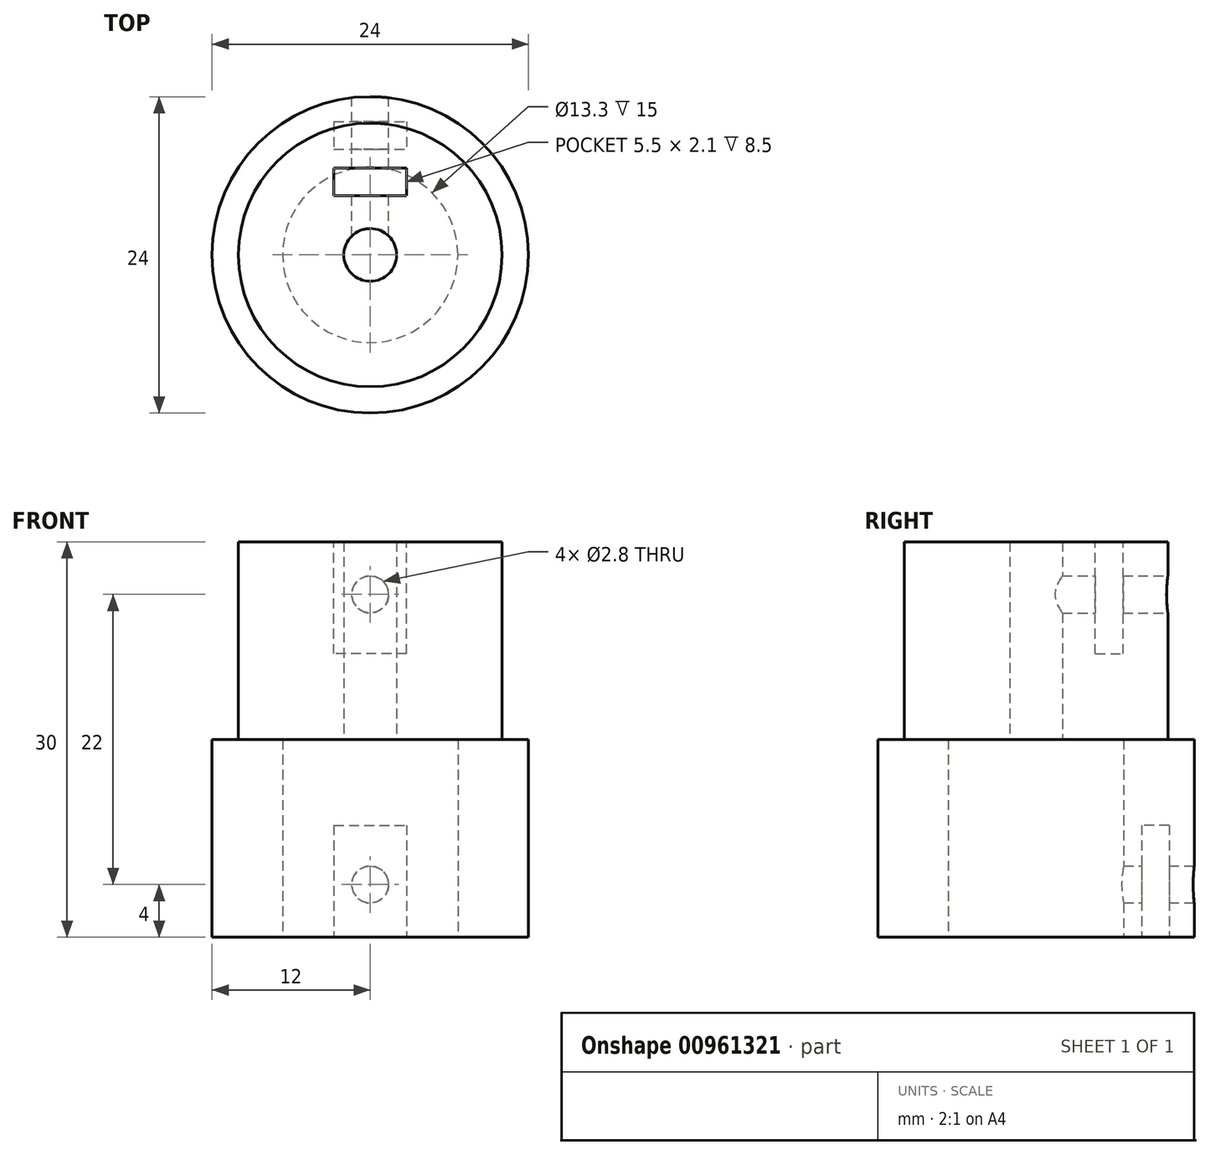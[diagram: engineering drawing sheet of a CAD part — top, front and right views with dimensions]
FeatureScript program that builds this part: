
annotation { "Feature Type Name" : "Feature", "Feature Type Description" : "" }
export const myFeature = defineFeature(function(context is Context, id is Id, definition is map)
    precondition{}
    {
        {
            var Q0;
            Q0=qCreatedBy(makeId("Top.planeOp"),FACE);
            var sketch = newSketch(context, id + "F0", { "sketchPlane" : qUnion([Q0])});
            skCircle(sketch, "E0", {"center": v(0, 0) * mm, "radius": 6.65 * mm});
            skCircle(sketch, "E1", {"center": v(0, 0) * mm, "radius": 12 * mm});
            skSolve(sketch);
        }
        {
            var Q0;
            Q0 = qSketchRegion(id + "F0", true);
            extrude(context, id + "F1", {"entities" : qUnion([Q0]), "depth" : 15 * mm, "offsetDistance" : 25 * mm});
        }
        {
            var Q0;
            Q0=qCreatedBy(makeId("Front.planeOp"),FACE);
            cPlane(context, id + "F2", {"entities" : qUnion([Q0]), "cplaneType" : CPlaneType.OFFSET, "offset" : 14 * mm, "oppositeDirection" : true, "width" : 150 * mm, "height" : 150 * mm});
        }
        {
            var Q0;
            Q0=qCreatedBy(id+"F2.planeOp",FACE);
            var sketch = newSketch(context, id + "F3", { "sketchPlane" : qUnion([Q0])});
            skCircle(sketch, "E2", {"center": v(0, 4) * mm, "radius": 1.4 * mm});
            skSolve(sketch);
        }
        {
            var Q0;
            Q0=makeQuery(id+"F3.imprint","IMPRINT",FACE,{"disambiguationData":[TD([[makeQuery(id+"F3.imprint","IMPRINT",EDGE,{"derivedFrom":sQuery(id+"F3.wireOp",EDGE,"E2")}),1.0]])]});
            var Q1;
            Q1=makeQuery(id+"F3.imprint","IMPRINT",FACE,{"disambiguationData":[TD([[makeQuery(id+"F3.imprint","IMPRINT",EDGE,{"derivedFrom":sQuery(id+"F3.wireOp",EDGE,"FONxLhb4-qUyD-SSOe-wBW2-8P9LQDapAw2D")}),1.0]])]});
            extrude(context, id + "F4", {"entities" : qUnion([Q0, Q1]), "operationType" : NewBodyOperationType.REMOVE, "depth" : 10 * mm, "offsetDistance" : 25 * mm});
        }
        {
            var Q0;
            Q0=makeQuery(id+"F1.opExtrude","CAP_FACE",FACE,{"disambiguationData":[OSD([sQuery(id+"F0.wireOp",EDGE,"E0"),sQuery(id+"F0.wireOp",EDGE,"E1")])],"isStart":false});
            var sketch = newSketch(context, id + "F5", { "sketchPlane" : qUnion([Q0])});
            skCircle(sketch, "E3", {"center": v(0, 0) * mm, "radius": 10 * mm});
            skCircle(sketch, "E4", {"center": v(0, 0) * mm, "radius": 2 * mm});
            skSolve(sketch);
        }
        {
            var Q0;
            Q0 = qSketchRegion(id + "F5", true);
            extrude(context, id + "F6", {"entities" : qUnion([Q0]), "operationType" : NewBodyOperationType.ADD, "depth" : 15 * mm, "offsetDistance" : 25 * mm});
        }
        {
            var Q0;
            Q0=qCreatedBy(makeId("Front.planeOp"),FACE);
            cPlane(context, id + "F7", {"entities" : qUnion([Q0]), "cplaneType" : CPlaneType.OFFSET, "offset" : 11.5 * mm, "oppositeDirection" : true, "width" : 150 * mm, "height" : 150 * mm});
        }
        {
            var Q0;
            Q0=qCreatedBy(id+"F7.planeOp",FACE);
            var sketch = newSketch(context, id + "F8", { "sketchPlane" : qUnion([Q0])});
            skCircle(sketch, "E5", {"center": v(0, 26) * mm, "radius": 1.4 * mm});
            skSolve(sketch);
        }
        {
            var Q0;
            Q0 = qSketchRegion(id + "F8", true);
            extrude(context, id + "F9", {"entities" : qUnion([Q0]), "operationType" : NewBodyOperationType.REMOVE, "depth" : 11 * mm, "offsetDistance" : 25 * mm});
        }
        {
            var Q0;
            Q0=makeQuery(id+"F6.opExtrude","CAP_FACE",FACE,{"disambiguationData":[OSD([sQuery(id+"F5.wireOp",EDGE,"E3"),sQuery(id+"F5.wireOp",EDGE,"E4")])],"isStart":false});
            var sketch = newSketch(context, id + "F10", { "sketchPlane" : qUnion([Q0])});
            skLineSegment(sketch, "E6.bottom", {"start": v(2.75, 4.5) * mm, "end": v(-2.75, 4.5) * mm});
            skLineSegment(sketch, "E6.top", {"start": v(2.75, 6.6) * mm, "end": v(-2.75, 6.6) * mm});
            skLineSegment(sketch, "E6.left", {"start": v(2.75, 4.5) * mm, "end": v(2.75, 6.6) * mm});
            skLineSegment(sketch, "E6.right", {"start": v(-2.75, 4.5) * mm, "end": v(-2.75, 6.6) * mm});
            skSolve(sketch);
        }
        {
            var Q0;
            Q0 = qSketchRegion(id + "F10", true);
            extrude(context, id + "F11", {"entities" : qUnion([Q0]), "operationType" : NewBodyOperationType.REMOVE, "oppositeDirection" : true, "depth" : 8.5 * mm, "offsetDistance" : 25 * mm});
        }
        {
            var Q0;
            Q0=makeQuery(id+"F0.imprint","IMPRINT",FACE,{"disambiguationData":[TD([[makeQuery(id+"F0.imprint","IMPRINT",EDGE,{"derivedFrom":sQuery(id+"F0.wireOp",EDGE,"E0")}),-1.0]])]});
            var sketch = newSketch(context, id + "F12", { "sketchPlane" : qUnion([Q0])});
            skLineSegment(sketch, "E7.bottom", {"start": v(-2.75, 10.1) * mm, "end": v(2.75, 10.1) * mm});
            skLineSegment(sketch, "E7.top", {"start": v(-2.75, 8) * mm, "end": v(2.75, 8) * mm});
            skLineSegment(sketch, "E7.left", {"start": v(-2.75, 10.1) * mm, "end": v(-2.75, 8) * mm});
            skLineSegment(sketch, "E7.right", {"start": v(2.75, 10.1) * mm, "end": v(2.75, 8) * mm});
            skSolve(sketch);
        }
        {
            var Q0;
            Q0 = qSketchRegion(id + "F12", true);
            extrude(context, id + "F13", {"entities" : qUnion([Q0]), "operationType" : NewBodyOperationType.REMOVE, "depth" : 8.5 * mm, "offsetDistance" : 25 * mm});
        }
    });
